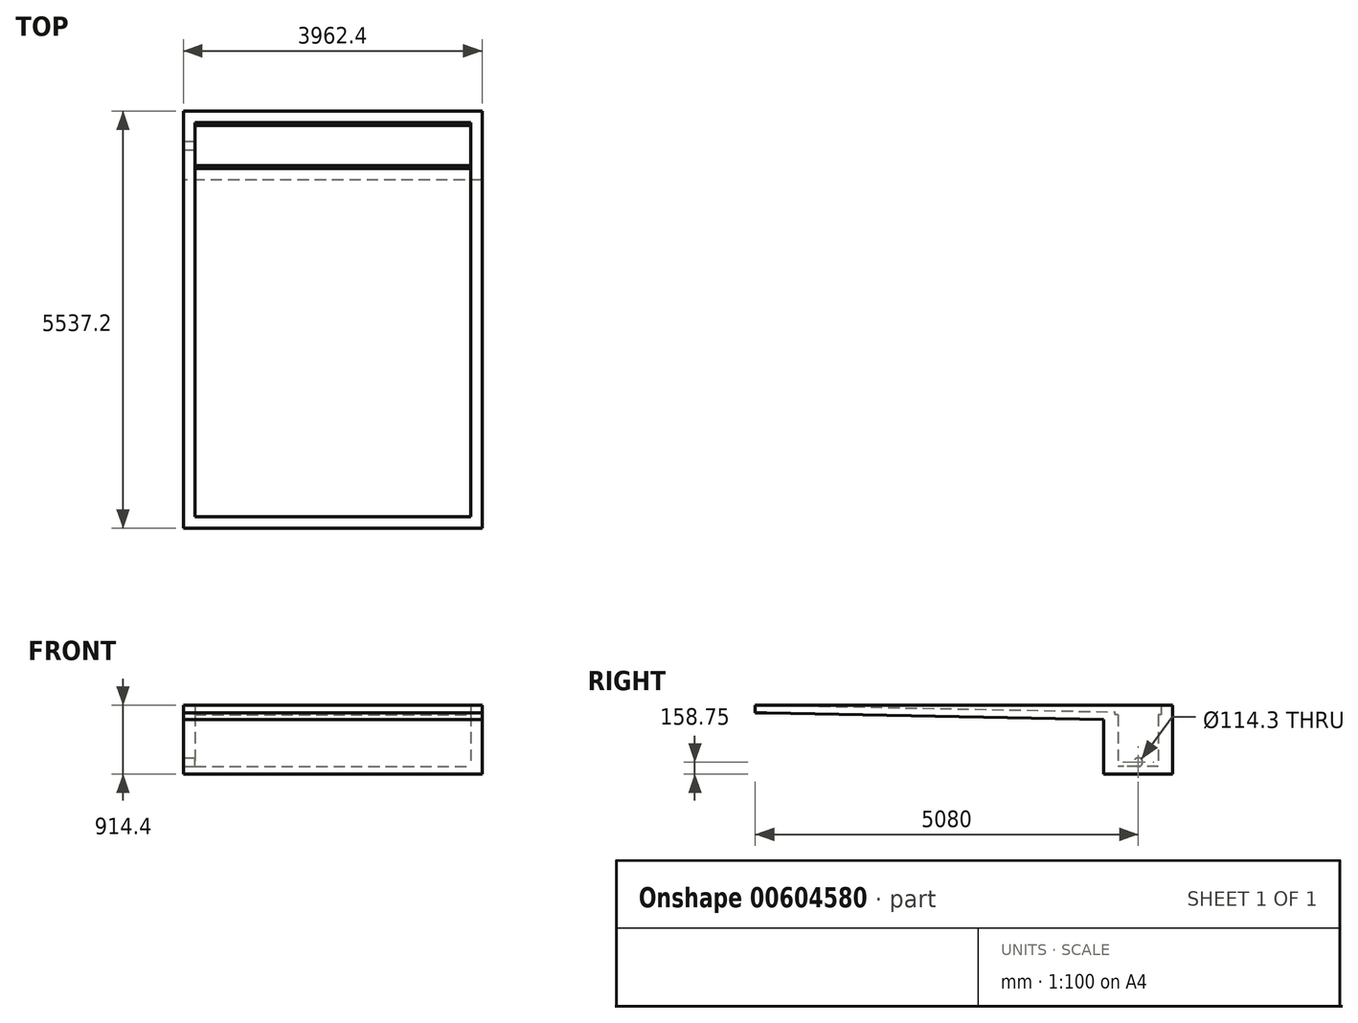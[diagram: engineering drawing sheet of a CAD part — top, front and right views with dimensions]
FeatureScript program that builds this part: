
annotation { "Feature Type Name" : "Feature", "Feature Type Description" : "" }
export const myFeature = defineFeature(function(context is Context, id is Id, definition is map)
    precondition{}
    {
        {
            var Q0;
            Q0=qCreatedBy(makeId("Top.planeOp"),FACE);
            var sketch = newSketch(context, id + "F0", { "sketchPlane" : qUnion([Q0])});
            skLineSegment(sketch, "E0.bottom", {"start": v(1981.2, 2692.4) * mm, "end": v(-1981.2, 2692.4) * mm});
            skLineSegment(sketch, "E0.top", {"start": v(1981.2, -2692.4) * mm, "end": v(-1981.2, -2692.4) * mm});
            skLineSegment(sketch, "E0.left", {"start": v(1981.2, 2692.4) * mm, "end": v(1981.2, -2692.4) * mm});
            skLineSegment(sketch, "E0.right", {"start": v(-1981.2, 2692.4) * mm, "end": v(-1981.2, -2692.4) * mm});
            skPoint(sketch, "E0.middle", {"position": v(0, 0) * mm});
            skSolve(sketch);
        }
        {
            var Q0;
            Q0 = qSketchRegion(id + "F0", true);
            extrude(context, id + "F1", {"entities" : qUnion([Q0]), "depth" : 203.2 * mm, "offsetDistance" : 25.4 * mm});
        }
        {
            var Q0;
            Q0=qCreatedBy(makeId("Right.planeOp"),FACE);
            var sketch = newSketch(context, id + "F2", { "sketchPlane" : qUnion([Q0])});
            skLineSegment(sketch, "E1", {"start": v(-2692.4, 203.2) * mm, "end": v(2540, 101.6) * mm});
            skLineSegment(sketch, "E2", {"start": v(2540, 101.6) * mm, "end": v(2540, 203.2) * mm});
            skLineSegment(sketch, "E3", {"start": v(2540, 203.2) * mm, "end": v(-2692.4, 203.2) * mm});
            skLineSegment(sketch, "E4", {"start": v(-2692.4, 101.6) * mm, "end": v(2540, 0) * mm});
            skLineSegment(sketch, "E5", {"start": v(2540, 0) * mm, "end": v(-2692.4, 0) * mm});
            skLineSegment(sketch, "E6", {"start": v(-2692.4, 0) * mm, "end": v(-2692.4, 101.6) * mm});
            skSolve(sketch);
        }
        {
            var Q0;
            Q0=makeQuery(id+"F1.opExtrude","SWEPT_FACE",FACE,{"disambiguationData":[OSD([sQuery(id+"F0.wireOp",EDGE,"E0.right")])]});
            var sketch = newSketch(context, id + "F3", { "sketchPlane" : qUnion([Q0])});
            skLineSegment(sketch, "E7.bottom", {"start": v(-2692.4, 203.2) * mm, "end": v(-1778, 203.2) * mm});
            skLineSegment(sketch, "E7.top", {"start": v(-2692.4, -711.2) * mm, "end": v(-1778, -711.2) * mm});
            skLineSegment(sketch, "E7.left", {"start": v(-2692.4, 203.2) * mm, "end": v(-2692.4, -711.2) * mm});
            skLineSegment(sketch, "E7.right", {"start": v(-1778, 203.2) * mm, "end": v(-1778, -711.2) * mm});
            skSolve(sketch);
        }
        {
            var Q0;
            Q0 = qSketchRegion(id + "F2", true);
            extrude(context, id + "F4", {"entities" : qUnion([Q0]), "operationType" : NewBodyOperationType.REMOVE, "endBound" : BoundingType.SYMMETRIC, "depth" : 3657.6 * mm, "offsetDistance" : 25.4 * mm});
        }
        {
            var Q0;
            Q0=makeQuery(id+"F4.boolean.opBoolean","COPY",FACE,{"derivedFrom":makeQuery(id+"F4.opExtrude","CAP_FACE",FACE,{"disambiguationData":[OSD([sQuery(id+"F2.wireOp",EDGE,"E4"),sQuery(id+"F2.wireOp",EDGE,"E5"),sQuery(id+"F2.wireOp",EDGE,"E6")])],"isStart":true})});
            extrude(context, id + "F5", {"entities" : qUnion([Q0]), "operationType" : NewBodyOperationType.REMOVE, "endBound" : BoundingType.THROUGH_ALL, "oppositeDirection" : true, "depth" : 25.4 * mm, "offsetDistance" : 25.4 * mm});
        }
        {
            var Q0;
            Q0=makeQuery(id+"F4.boolean.opBoolean","COPY",FACE,{"derivedFrom":makeQuery(id+"F4.opExtrude","CAP_FACE",FACE,{"disambiguationData":[OSD([sQuery(id+"F2.wireOp",EDGE,"E4"),sQuery(id+"F2.wireOp",EDGE,"E5"),sQuery(id+"F2.wireOp",EDGE,"E6")])],"isStart":false})});
            extrude(context, id + "F6", {"entities" : qUnion([Q0]), "operationType" : NewBodyOperationType.REMOVE, "endBound" : BoundingType.THROUGH_ALL, "oppositeDirection" : true, "depth" : 25.4 * mm, "offsetDistance" : 25.4 * mm});
        }
        {
            var Q0;
            Q0 = qSketchRegion(id + "F3", true);
            var Q1;
            Q1=makeQuery(id+"F1.opExtrude","SWEPT_FACE",FACE,{"disambiguationData":[OSD([sQuery(id+"F0.wireOp",EDGE,"E0.left")])]});
            extrude(context, id + "F7", {"entities" : qUnion([Q0]), "operationType" : NewBodyOperationType.ADD, "endBound" : BoundingType.UP_TO_SURFACE, "oppositeDirection" : true, "depth" : 25.4 * mm, "endBoundEntityFace" : qUnion([Q1]), "offsetDistance" : 25.4 * mm});
        }
        {
            var Q0;
            Q0=makeQuery(id+"F2.imprint","IMPRINT",FACE,{"disambiguationData":[TD([[makeQuery(id+"F2.imprint","IMPRINT",EDGE,{"derivedFrom":sQuery(id+"F2.wireOp",EDGE,"E1")}),1.0]])]});
            var Q1;
            Q1=makeQuery(id+"F4.boolean.opBoolean","COPY",FACE,{"derivedFrom":makeQuery(id+"F4.opExtrude","CAP_FACE",FACE,{"disambiguationData":[OSD([sQuery(id+"F2.wireOp",EDGE,"E1"),sQuery(id+"F2.wireOp",EDGE,"E2"),sQuery(id+"F2.wireOp",EDGE,"E3")])],"isStart":true})});
            var Q2;
            Q2=makeQuery(id+"F4.boolean.opBoolean","COPY",FACE,{"derivedFrom":makeQuery(id+"F4.opExtrude","CAP_FACE",FACE,{"disambiguationData":[OSD([sQuery(id+"F2.wireOp",EDGE,"E1"),sQuery(id+"F2.wireOp",EDGE,"E2"),sQuery(id+"F2.wireOp",EDGE,"E3")])],"isStart":false})});
            extrude(context, id + "F8", {"entities" : qUnion([Q0]), "operationType" : NewBodyOperationType.REMOVE, "endBound" : BoundingType.UP_TO_SURFACE, "oppositeDirection" : true, "depth" : 25.4 * mm, "endBoundEntityFace" : qUnion([Q1]), "offsetDistance" : 25.4 * mm, "hasSecondDirection" : true, "secondDirectionBound" : SecondDirectionBoundingType.UP_TO_SURFACE, "secondDirectionOppositeDirection" : false, "secondDirectionDepth" : 25.4 * mm, "secondDirectionBoundEntityFace" : qUnion([Q2])});
        }
        {
            var Q0;
            Q0=makeQuery(id+"F7.boolean.opBoolean","MERGE",FACE,{"derivedFrom":[makeQuery(id+"F1.opExtrude","CAP_FACE",FACE,{"disambiguationData":[OSD([sQuery(id+"F0.wireOp",EDGE,"E0.bottom"),sQuery(id+"F0.wireOp",EDGE,"E0.top"),sQuery(id+"F0.wireOp",EDGE,"E0.left"),sQuery(id+"F0.wireOp",EDGE,"E0.right")])],"isStart":false}),makeQuery(id+"F7.opExtrude","SWEPT_FACE",FACE,{"disambiguationData":[OSD([sQuery(id+"F3.wireOp",EDGE,"E7.bottom")])]})]});
            var sketch = newSketch(context, id + "F9", { "sketchPlane" : qUnion([Q0])});
            skLineSegment(sketch, "E8.bottom", {"start": v(-1828.8, 2540) * mm, "end": v(1828.8, 2540) * mm});
            skLineSegment(sketch, "E8.top", {"start": v(-1828.8, 1930.4) * mm, "end": v(1828.8, 1930.4) * mm});
            skLineSegment(sketch, "E8.left", {"start": v(-1828.8, 2540) * mm, "end": v(-1828.8, 1930.4) * mm});
            skLineSegment(sketch, "E8.right", {"start": v(1828.8, 2540) * mm, "end": v(1828.8, 1930.4) * mm});
            skSolve(sketch);
        }
        {
            var Q0;
            Q0 = qSketchRegion(id + "F9", true);
            var Q1;
            Q1=makeQuery(id+"F7.opExtrude","SWEPT_FACE",FACE,{"disambiguationData":[OSD([sQuery(id+"F3.wireOp",EDGE,"E7.top")])]});
            extrude(context, id + "F10", {"entities" : qUnion([Q0]), "operationType" : NewBodyOperationType.REMOVE, "endBound" : BoundingType.UP_TO_SURFACE, "oppositeDirection" : true, "depth" : 25.4 * mm, "endBoundEntityFace" : qUnion([Q1]), "hasOffset" : true, "offsetDistance" : 101.6 * mm});
        }
        {
            var Q0;
            Q0=makeQuery(id+"F10.boolean.opBoolean","COPY",FACE,{"derivedFrom":makeQuery(id+"F10.opExtrude","CAP_FACE",FACE,{"disambiguationData":[OSD([sQuery(id+"F9.wireOp",EDGE,"E8.bottom"),sQuery(id+"F9.wireOp",EDGE,"E8.top"),sQuery(id+"F9.wireOp",EDGE,"E8.left"),sQuery(id+"F9.wireOp",EDGE,"E8.right")])],"isStart":false})});
            var sketch = newSketch(context, id + "F11", { "sketchPlane" : qUnion([Q0])});
            skLineSegment(sketch, "E9.bottom", {"start": v(1828.8, 2540) * mm, "end": v(-1828.8, 2540) * mm});
            skLineSegment(sketch, "E9.top", {"start": v(1828.8, 2501.9) * mm, "end": v(-1828.8, 2501.9) * mm});
            skLineSegment(sketch, "E9.left", {"start": v(1828.8, 2540) * mm, "end": v(1828.8, 2501.9) * mm});
            skLineSegment(sketch, "E9.right", {"start": v(-1828.8, 2540) * mm, "end": v(-1828.8, 2501.9) * mm});
            skLineSegment(sketch, "E10.bottom", {"start": v(-1828.8, 1930.4) * mm, "end": v(1828.8, 1930.4) * mm});
            skLineSegment(sketch, "E10.top", {"start": v(-1828.8, 1968.5) * mm, "end": v(1828.8, 1968.5) * mm});
            skLineSegment(sketch, "E10.left", {"start": v(-1828.8, 1930.4) * mm, "end": v(-1828.8, 1968.5) * mm});
            skLineSegment(sketch, "E10.right", {"start": v(1828.8, 1930.4) * mm, "end": v(1828.8, 1968.5) * mm});
            skSolve(sketch);
        }
        {
            var Q0;
            Q0 = qSketchRegion(id + "F11", true);
            var Q1;
            {var subQ0=sQuery(id+"F2.wireOp",EDGE,"E1");Q1=makeQuery(id+"F10.boolean.opBoolean","INTERSECT",VERTEX,{"disambiguationData":[OD(1.0)],"derivedFrom":[makeQuery(id+"F8.boolean.opBoolean","MERGE",FACE,{"derivedFrom":[makeQuery(id+"F4.boolean.opBoolean","COPY",FACE,{"derivedFrom":makeQuery(id+"F4.opExtrude","SWEPT_FACE",FACE,{"disambiguationData":[OSD([subQ0])]})})],"fromTools":[makeQuery(id+"F8.opExtrude","SWEPT_FACE",FACE,{"disambiguationData":[OSD([subQ0])]})]}),makeQuery(id+"F10.opExtrude","SWEPT_FACE",FACE,{"disambiguationData":[OSD([sQuery(id+"F9.wireOp",EDGE,"E8.top")])]})]});}
            extrude(context, id + "F12", {"entities" : qUnion([Q0]), "operationType" : NewBodyOperationType.ADD, "endBound" : BoundingType.UP_TO_VERTEX, "depth" : 25.4 * mm, "endBoundEntityVertex" : qUnion([Q1]), "hasOffset" : true, "offsetDistance" : 38.1 * mm});
        }
        {
            var Q0;
            {var subQ0=sQuery(id+"F2.wireOp",EDGE,"E3");var subQ1=sQuery(id+"F2.wireOp",EDGE,"E2");var subQ2=sQuery(id+"F2.wireOp",EDGE,"E1");Q0=makeQuery(id+"F10.boolean.opBoolean","MERGE",FACE,{"derivedFrom":[makeQuery(id+"F8.boolean.opBoolean","MERGE",FACE,{"derivedFrom":[makeQuery(id+"F4.boolean.opBoolean","COPY",FACE,{"derivedFrom":makeQuery(id+"F4.opExtrude","CAP_FACE",FACE,{"disambiguationData":[OSD([subQ2,subQ1,subQ0])],"isStart":true})})],"fromTools":[makeQuery(id+"F8.opExtrude","CAP_FACE",FACE,{"disambiguationData":[OSD([subQ2,subQ1,subQ0])],"isStart":false})]})],"fromTools":[makeQuery(id+"F10.opExtrude","SWEPT_FACE",FACE,{"disambiguationData":[OSD([sQuery(id+"F9.wireOp",EDGE,"E8.left")])]})]});}
            var sketch = newSketch(context, id + "F13", { "sketchPlane" : qUnion([Q0])});
            skCircle(sketch, "E11", {"center": v(2235.2, -552.45) * mm, "radius": 57.15 * mm});
            skLineSegment(sketch, "E12", {"start": v(2235.2, -552.45) * mm, "end": v(2235.2, -609.6) * mm, "construction": true});
            skSolve(sketch);
        }
        {
            var Q0;
            Q0 = qSketchRegion(id + "F13", true);
            extrude(context, id + "F14", {"entities" : qUnion([Q0]), "operationType" : NewBodyOperationType.REMOVE, "endBound" : BoundingType.THROUGH_ALL, "oppositeDirection" : true, "depth" : 25.4 * mm, "offsetDistance" : 25.4 * mm});
        }
        {
            var Q0;
            Q0=makeQuery(id+"F1.opExtrude","SWEPT_FACE",FACE,{"disambiguationData":[OSD([sQuery(id+"F0.wireOp",EDGE,"E0.top")])]});
            extrude(context, id + "F15", {"entities" : qUnion([Q0]), "operationType" : NewBodyOperationType.ADD, "depth" : 152.4 * mm, "offsetDistance" : 25.4 * mm});
        }
    });
